# Revit family: Domotics-DomesticRanges-GEWISS-SYSTEM_COMMAND-PUSH-BUTTON_NAME_PLATE
name_source: partatom
category: Apparecchi elettrici
revit_build: Autodesk Revit 2016 (Build: 20161004_0715(x64)
units: mm (PartAtom-declared; Revit-internal decimal feet)

## family parameters
Condiviso = Sì
Host = Superficie
Mantenere orientamento annotazione = Sì
Numero OmniClass = 23.80.50.11.14
Punto di calcolo locali = Sì
Quota connettore circolare = Usa diametro
Taglio con vuoti quando caricato = Sì
Tipo di parte = Normale
Titolo OmniClass = Switches

## types (4) — shared parameters
Bidimensionale = BIDIMENSIONALE SYSTEM PULSANTE TARGA : 2P
Carico apparente = 0 VA
Catalogue = DOMOTICS
Catalogue Range = SYSTEM - DOMESTIC RANGE
Description. = Push-button with name plate
Description: = 1P NO - 10A
Electrocod = 0130
IDF = 809d39ac-d065-436b-a420-7a8d7026f49b
IDT = acf20124-4b05-42a8-9547-f2406c89ff56
Immagine tipo = GW21591.jpg
Lamp = Cartridge lamp S6x36 mm
Lamp power = 2W
Lamp voltage = 12-24V ac/dc
Lamp voltage: = 12-24V
Larghezza pulsante = 46 mm  [stored 0.150919 ft]
N. poli = 1
Produttore = GEWISS S.p.A.
Prospetto di default = 1219 mm
SEO = Push button
Simbolo = SIMBOLO PULSANTI : TARGA
Technical sheet = https://www.gewiss.com
Tipo_ = SYSTEM PULSANTI TARGA_BASE : NERO 2P
Type = Illuminable
Type of lamp = Cartridge lamp S6x36 mm
Type: = Name plate
URL = https://www.gewiss.com
Version file RFA = 19.4
Volt = 230 V
Voltage = 250 V ac
Voltage: = 250 V ac

## per-type parameters (varying)
| type | Colour | Descrizione | EAN code | Modello | No. SYSTEM modules |
| GW20591 - Push-button-name plate 2M illum.white | White | PUSH-BUTTON-NAME PLATE 2M ILLUM.SY/WT | 8011564077379 | GW20591 | 2 |
| GW21591 - Push-button-name plate 2M illum.black | Black | PUSH-BUTTON-NAME PLATE 2M ILLUM.SY/BK | 8011564128194 | GW21591 | 2 |
| GW21024 - Push-button-name plate 3M illum.black | Black | PUSH-BUTTON-NAME PLATE 3M ILLUM.SY/BK | 8011564128200 | GW21024 | 3 |
| GW20024 - Push-button-name plate 3M illum.white | White | PUSH-BUTTON-NAME PLATE 3M ILLUM.SY/WT | 8011564000346 | GW20024 | 3 |

note: [stored X ft] marks values corroborated as IEEE doubles in the binary element streams (Revit-internal decimal feet)

## geometry (parser evidence)
native form markers: Sweep x1
no freeform markers — native parametric forms only
